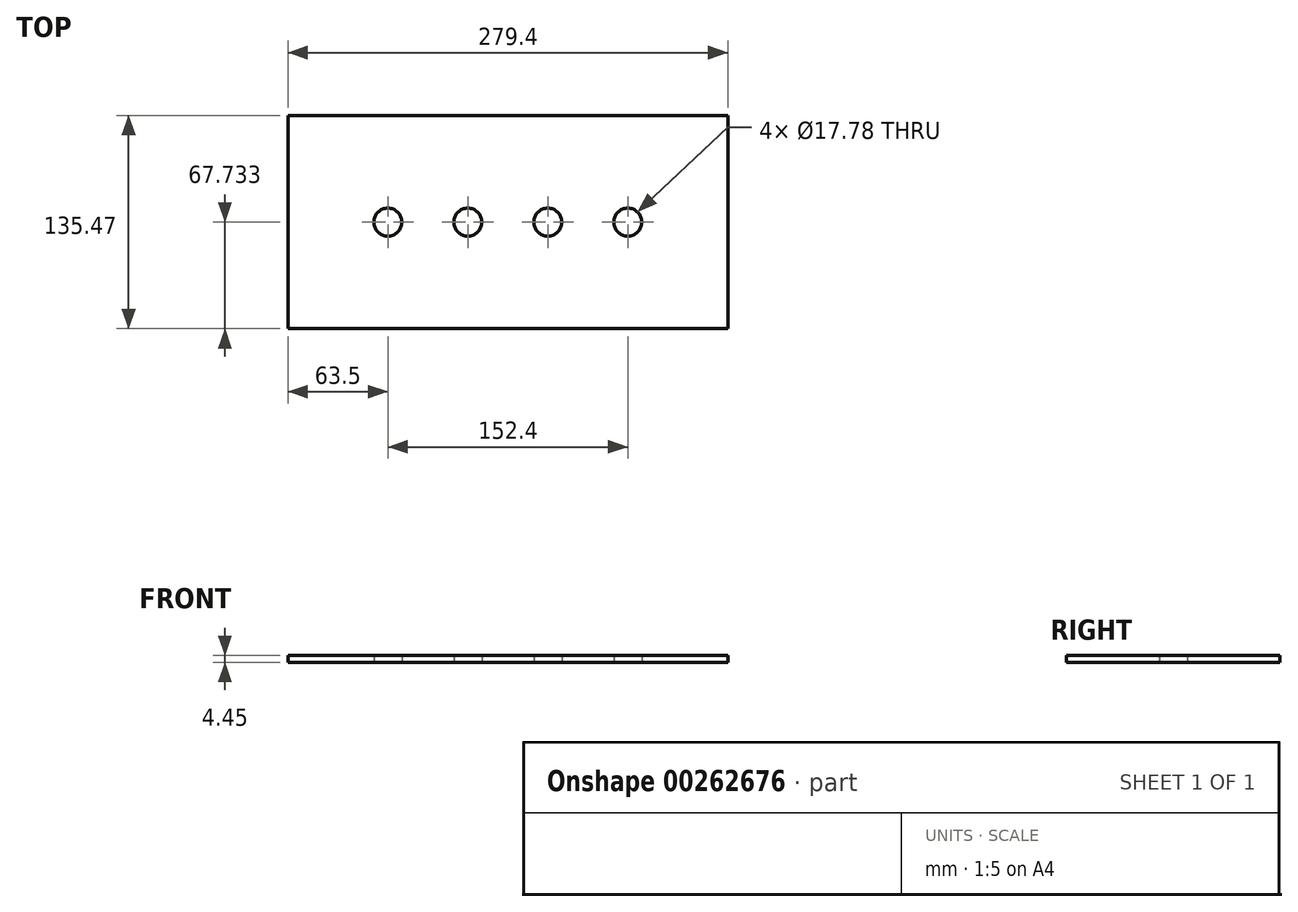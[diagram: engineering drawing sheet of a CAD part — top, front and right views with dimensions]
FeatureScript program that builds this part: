
annotation { "Feature Type Name" : "Feature", "Feature Type Description" : "" }
export const myFeature = defineFeature(function(context is Context, id is Id, definition is map)
    precondition{}
    {
        {
            var Q0;
            Q0=qCreatedBy(makeId("Top.planeOp"),FACE);
            var sketch = newSketch(context, id + "F0", { "sketchPlane" : qUnion([Q0])});
            skLineSegment(sketch, "E0.bottom", {"start": v(0, 0) * mm, "end": v(279.4, 0) * mm});
            skLineSegment(sketch, "E0.top", {"start": v(0, 135.47) * mm, "end": v(279.4, 135.47) * mm});
            skLineSegment(sketch, "E0.left", {"start": v(0, 0) * mm, "end": v(0, 135.47) * mm});
            skLineSegment(sketch, "E0.right", {"start": v(279.4, 0) * mm, "end": v(279.4, 135.47) * mm});
            skCircle(sketch, "E1", {"center": v(63.5, 67.73) * mm, "radius": 8.89 * mm});
            skPoint(sketch, "E1.centerSnap0", {"position": v(0, 67.73) * mm});
            skCircle(sketch, "E2", {"center": v(114.3, 67.73) * mm, "radius": 8.9 * mm});
            skCircle(sketch, "E3", {"center": v(165.1, 67.73) * mm, "radius": 8.9 * mm});
            skCircle(sketch, "E4", {"center": v(215.9, 67.73) * mm, "radius": 8.9 * mm});
            skSolve(sketch);
        }
        {
            var Q0;
            Q0=makeQuery(id+"F0.imprint","IMPRINT",FACE,{"disambiguationData":[TD([[makeQuery(id+"F0.imprint","IMPRINT",EDGE,{"derivedFrom":sQuery(id+"F0.wireOp",EDGE,"E0.bottom")}),1.0]])]});
            extrude(context, id + "F1", {"entities" : qUnion([Q0]), "depth" : 4.44 * mm});
        }
    });
